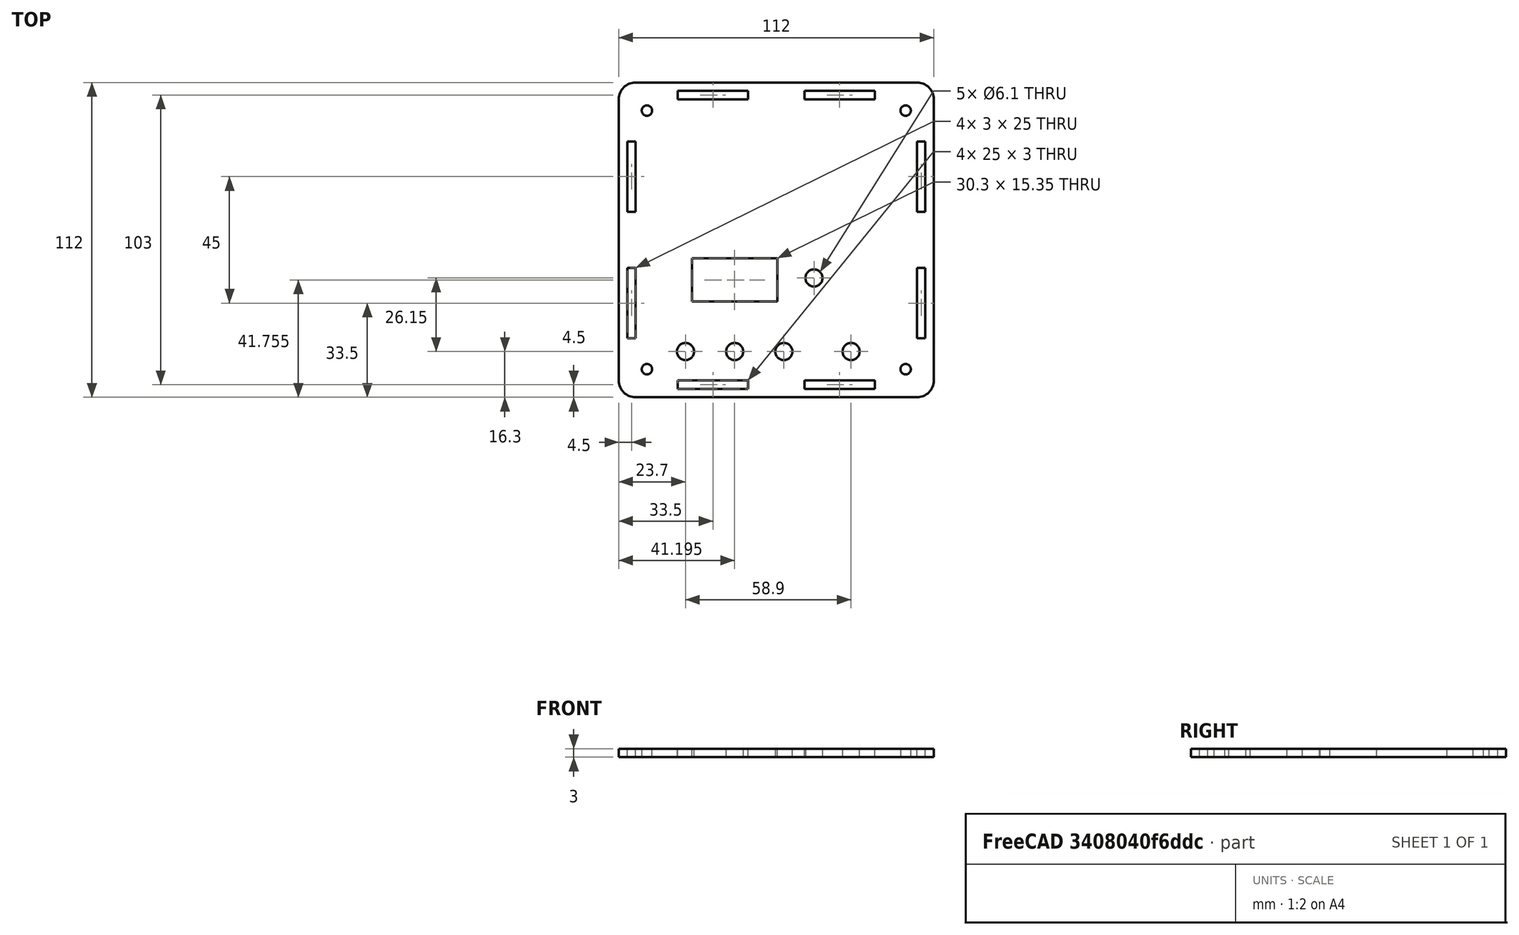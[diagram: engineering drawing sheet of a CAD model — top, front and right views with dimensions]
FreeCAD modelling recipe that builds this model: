
FCSTD DOCUMENT  (FreeCAD 0.19R24267 +99 (Git))
Label: top
License: All rights reserved
LicenseURL: http://en.wikipedia.org/wiki/All_rights_reserved
objects: App::Part×1, Sketcher::SketchObject×1, Part::Extrusion×1
note: 2 computed .brp shape members not serialized (recipe doc carries the construction recipe); baked Part::Feature solids carry a one-line shape summary decoded from their .brp

FEATURE [App::Part] Part
  Origin = -> Origin
FEATURE [Sketcher::SketchObject] Sketch
  FullyConstrained = true
  sketch-geometry (57):
    g0: LineSegment StartX=0 StartY=0 StartZ=0 EndX=100 EndY=0 EndZ=0
    g1: LineSegment StartX=100 StartY=0 StartZ=0 EndX=100 EndY=100 EndZ=0
    g2: LineSegment StartX=100 StartY=100 StartZ=0 EndX=0 EndY=100 EndZ=0
    g3: LineSegment StartX=0 StartY=100 StartZ=0 EndX=0 EndY=0 EndZ=0
    g4: Circle CenterX=17.7 CenterY=10.3 CenterZ=0 NormalX=0 NormalY=0 NormalZ=1 AngleXU=0 Radius=3.05
    g5: Circle CenterX=35.2 CenterY=10.3 CenterZ=0 NormalX=0 NormalY=0 NormalZ=1 AngleXU=0 Radius=3.05
    g6: Circle CenterX=52.7 CenterY=10.3 CenterZ=0 NormalX=0 NormalY=0 NormalZ=1 AngleXU=0 Radius=3.05
    g7: Circle CenterX=76.6 CenterY=10.3 CenterZ=0 NormalX=0 NormalY=0 NormalZ=1 AngleXU=0 Radius=3.05
    g8: Circle CenterX=63.4 CenterY=36.45 CenterZ=0 NormalX=0 NormalY=0 NormalZ=1 AngleXU=0 Radius=3.05
    g9: LineSegment StartX=20.045 StartY=43.43 StartZ=0 EndX=50.345 EndY=43.43 EndZ=0
    g10: LineSegment StartX=50.345 StartY=43.43 StartZ=0 EndX=50.345 EndY=28.08 EndZ=0
    g11: LineSegment StartX=50.345 StartY=28.08 StartZ=0 EndX=20.045 EndY=28.08 EndZ=0
    g12: LineSegment StartX=20.045 StartY=28.08 StartZ=0 EndX=20.045 EndY=43.43 EndZ=0
    g13: ArcOfCircle CenterX=0 CenterY=100 CenterZ=0 NormalX=0 NormalY=0 NormalZ=1 AngleXU=0 Radius=6 StartAngle=1.5708 EndAngle=3.14159
    g14: ArcOfCircle CenterX=100 CenterY=100 CenterZ=0 NormalX=0 NormalY=0 NormalZ=1 AngleXU=0 Radius=6 StartAngle=0 EndAngle=1.5708
    g15: LineSegment StartX=0 StartY=106 StartZ=0 EndX=100 EndY=106 EndZ=0
    g16: Circle CenterX=4 CenterY=96 CenterZ=0 NormalX=0 NormalY=0 NormalZ=1 AngleXU=0 Radius=1.85
    g17: Circle CenterX=96 CenterY=96 CenterZ=0 NormalX=0 NormalY=0 NormalZ=1 AngleXU=0 Radius=1.85
    g18: Circle CenterX=96 CenterY=4 CenterZ=0 NormalX=0 NormalY=0 NormalZ=1 AngleXU=0 Radius=1.85
    g19: Circle CenterX=4 CenterY=4 CenterZ=0 NormalX=0 NormalY=0 NormalZ=1 AngleXU=0 Radius=1.85
    g20: ArcOfCircle CenterX=0 CenterY=0 CenterZ=0 NormalX=0 NormalY=0 NormalZ=1 AngleXU=0 Radius=6 StartAngle=3.14159 EndAngle=4.71239
    g21: ArcOfCircle CenterX=100 CenterY=0 CenterZ=0 NormalX=0 NormalY=0 NormalZ=1 AngleXU=0 Radius=6 StartAngle=4.71239 EndAngle=6.28319
    g22: LineSegment StartX=0 StartY=-6 StartZ=0 EndX=100 EndY=-6 EndZ=0
    g23: LineSegment StartX=106 StartY=-1.5e-15 StartZ=0 EndX=106 EndY=100 EndZ=0
    g24: LineSegment StartX=-6 StartY=100 StartZ=0 EndX=-6 EndY=0 EndZ=0
    g25: LineSegment StartX=15 StartY=100 StartZ=0 EndX=40 EndY=100 EndZ=0
    g26: LineSegment StartX=40 StartY=100 StartZ=0 EndX=40 EndY=103 EndZ=0
    g27: LineSegment StartX=40 StartY=103 StartZ=0 EndX=15 EndY=103 EndZ=0
    g28: LineSegment StartX=15 StartY=103 StartZ=0 EndX=15 EndY=100 EndZ=0
    g29: LineSegment StartX=60 StartY=100 StartZ=0 EndX=85 EndY=100 EndZ=0
    g30: LineSegment StartX=85 StartY=100 StartZ=0 EndX=85 EndY=103 EndZ=0
    g31: LineSegment StartX=85 StartY=103 StartZ=0 EndX=60 EndY=103 EndZ=0
    g32: LineSegment StartX=60 StartY=103 StartZ=0 EndX=60 EndY=100 EndZ=0
    g33: LineSegment StartX=100 StartY=85 StartZ=0 EndX=103 EndY=85 EndZ=0
    g34: LineSegment StartX=103 StartY=85 StartZ=0 EndX=103 EndY=60 EndZ=0
    g35: LineSegment StartX=103 StartY=60 StartZ=0 EndX=100 EndY=60 EndZ=0
    g36: LineSegment StartX=100 StartY=60 StartZ=0 EndX=100 EndY=85 EndZ=0
    g37: LineSegment StartX=100 StartY=40 StartZ=0 EndX=103 EndY=40 EndZ=0
    g38: LineSegment StartX=103 StartY=40 StartZ=0 EndX=103 EndY=15 EndZ=0
    g39: LineSegment StartX=103 StartY=15 StartZ=0 EndX=100 EndY=15 EndZ=0
    g40: LineSegment StartX=100 StartY=15 StartZ=0 EndX=100 EndY=40 EndZ=0
    g41: LineSegment StartX=85 StartY=0 StartZ=0 EndX=60 EndY=0 EndZ=0
    g42: LineSegment StartX=60 StartY=0 StartZ=0 EndX=60 EndY=-3 EndZ=0
    g43: LineSegment StartX=60 StartY=-3 StartZ=0 EndX=85 EndY=-3 EndZ=0
    g44: LineSegment StartX=85 StartY=-3 StartZ=0 EndX=85 EndY=0 EndZ=0
    g45: LineSegment StartX=40 StartY=0 StartZ=0 EndX=15 EndY=0 EndZ=0
    g46: LineSegment StartX=15 StartY=0 StartZ=0 EndX=15 EndY=-3 EndZ=0
    g47: LineSegment StartX=15 StartY=-3 StartZ=0 EndX=40 EndY=-3 EndZ=0
    g48: LineSegment StartX=40 StartY=-3 StartZ=0 EndX=40 EndY=0 EndZ=0
    g49: LineSegment StartX=0 StartY=15 StartZ=0 EndX=-3 EndY=15 EndZ=0
    g50: LineSegment StartX=-3 StartY=15 StartZ=0 EndX=-3 EndY=40 EndZ=0
    g51: LineSegment StartX=-3 StartY=40 StartZ=0 EndX=0 EndY=40 EndZ=0
    g52: LineSegment StartX=0 StartY=40 StartZ=0 EndX=0 EndY=15 EndZ=0
    g53: LineSegment StartX=0 StartY=85 StartZ=0 EndX=-3 EndY=85 EndZ=0
    g54: LineSegment StartX=-3 StartY=85 StartZ=0 EndX=-3 EndY=60 EndZ=0
    g55: LineSegment StartX=-3 StartY=60 StartZ=0 EndX=0 EndY=60 EndZ=0
    g56: LineSegment StartX=0 StartY=60 StartZ=0 EndX=0 EndY=85 EndZ=0
  constraints (170):
    c: Coincident(g0,g1)
    c: Coincident(g1,g2)
    c: Coincident(g2,g3)
    c: Coincident(g3,g0)
    c: Horizontal(g0)
    c: Horizontal(g2)
    c: Vertical(g1)
    c: Vertical(g3)
    c: Coincident(g0,g-1)
    c: DistanceX(g2,g2) = 100
    c: DistanceY(g1,g1) = 100
    c: Coincident(g9,g10)
    c: Coincident(g10,g11)
    c: Coincident(g11,g12)
    c: Coincident(g12,g9)
    c: Horizontal(g9)
    c: Horizontal(g11)
    c: Vertical(g10)
    c: Vertical(g12)
    c: DistanceX(g9,g9) = 30.3
    c: DistanceY(g12,g12) = 15.35
    c: DistanceX(g2,g9) = 20.045
    c: DistanceY(g9,g2) = 56.57
    c: Equal(g4,g5)
    c: Equal(g5,g6)
    c: Equal(g6,g7)
    c: DistanceX(g2,g8) = 63.4
    c: DistanceY(g8,g2) = 63.55
    c: Horizontal(g4,g5)
    c: Horizontal(g5,g6)
    c: Horizontal(g6,g7)
    c: DistanceX(g2,g4) = 17.7
    c: DistanceY(g4,g2) = 89.7
    c: DistanceX(g4,g5) = 17.5
    c: DistanceX(g5,g6) = 17.5
    c: DistanceX(g6,g7) = 23.9
    c: Radius(g8) = 3.05
    c: Radius(g7) = 3.05
    c: Coincident(g13,g2)
    c: PointOnObject(g13,g-2)
    c: Horizontal(g13,g13)
    c: Radius(g13) = 6
    c: Coincident(g14,g1)
    c: Radius(g14) = 6
    c: Vertical(g14,g14)
    c: Horizontal(g14,g14)
    c: Coincident(g15,g13)
    c: Coincident(g15,g14)
    c: Equal(g17,g16)
    c: Equal(g16,g19)
    c: Equal(g19,g18)
    c: Radius(g16) = 1.85
    c: Horizontal(g16,g17)
    c: Horizontal(g19,g18)
    c: Vertical(g19,g16)
    c: Vertical(g17,g18)
    c: DistanceX(g13,g16) = 4
    c: DistanceY(g16,g13) = 4
    c: DistanceY(g-1,g19) = 4
    c: DistanceX(g17,g14) = 4
    c: Coincident(g20,g-1)
    c: PointOnObject(g20,g-1)
    c: PointOnObject(g20,g-2)
    c: Radius(g20) = 6
    c: Coincident(g21,g0)
    c: PointOnObject(g21,g-1)
    c: Radius(g21) = 6
    c: Vertical(g21,g21)
    c: Coincident(g22,g20)
    c: Coincident(g22,g21)
    c: Coincident(g23,g21)
    c: Coincident(g23,g14)
    c: Coincident(g24,g13)
    c: Coincident(g24,g20)
    c: Coincident(g25,g26)
    c: Coincident(g26,g27)
    c: Coincident(g27,g28)
    c: Coincident(g28,g25)
    c: Horizontal(g25)
    c: Horizontal(g27)
    c: Vertical(g26)
    c: Vertical(g28)
    c: PointOnObject(g25,g2)
    c: Coincident(g29,g30)
    c: Coincident(g30,g31)
    c: Coincident(g31,g32)
    c: Coincident(g32,g29)
    c: Horizontal(g29)
    c: Horizontal(g31)
    c: Vertical(g30)
    c: Vertical(g32)
    c: PointOnObject(g29,g2)
    c: Coincident(g33,g34)
    c: Coincident(g34,g35)
    c: Coincident(g35,g36)
    c: Coincident(g36,g33)
    c: Horizontal(g33)
    c: Horizontal(g35)
    c: Vertical(g34)
    c: Vertical(g36)
    c: PointOnObject(g33,g1)
    c: Coincident(g37,g38)
    c: Coincident(g38,g39)
    c: Coincident(g39,g40)
    c: Coincident(g40,g37)
    c: Horizontal(g37)
    c: Horizontal(g39)
    c: Vertical(g38)
    c: Vertical(g40)
    c: PointOnObject(g37,g1)
    c: Coincident(g41,g42)
    c: Coincident(g42,g43)
    c: Coincident(g43,g44)
    c: Coincident(g44,g41)
    c: Horizontal(g41)
    c: Horizontal(g43)
    c: Vertical(g42)
    c: Vertical(g44)
    c: PointOnObject(g41,g0)
    c: Coincident(g45,g46)
    c: Coincident(g46,g47)
    c: Coincident(g47,g48)
    c: Coincident(g48,g45)
    c: Horizontal(g45)
    c: Horizontal(g47)
    c: Vertical(g46)
    c: Vertical(g48)
    c: PointOnObject(g45,g0)
    c: Coincident(g49,g50)
    c: Coincident(g50,g51)
    c: Coincident(g51,g52)
    c: Coincident(g52,g49)
    c: Horizontal(g49)
    c: Horizontal(g51)
    c: Vertical(g50)
    c: Vertical(g52)
    c: Coincident(g53,g54)
    c: Coincident(g54,g55)
    c: Coincident(g55,g56)
    c: Coincident(g56,g53)
    c: Horizontal(g53)
    c: Horizontal(g55)
    c: Vertical(g54)
    c: Vertical(g56)
    c: PointOnObject(g53,g3)
    c: Equal(g28,g32)
    c: Equal(g32,g53)
    c: Equal(g53,g33)
    c: Equal(g33,g37)
    c: Equal(g37,g51)
    c: Equal(g51,g48)
    c: Equal(g48,g42)
    c: DistanceY(g48,g48) = 3
    c: Equal(g47,g43)
    c: Equal(g43,g38)
    c: Equal(g38,g50)
    c: Equal(g50,g34)
    c: Equal(g34,g54)
    c: Equal(g54,g27)
    c: Equal(g27,g31)
    c: DistanceX(g27,g27) = 25
    c: DistanceX(g13,g27) = 15
    c: DistanceX(g30,g14) = 15
    c: DistanceY(g33,g14) = 15
    c: DistanceY(g21,g39) = 15
    c: DistanceX(g43,g21) = 15
    c: DistanceX(g20,g46) = 15
    c: DistanceY(g20,g49) = 15
    c: DistanceY(g53,g13) = 15
    c: PointOnObject(g49,g3)
FEATURE [Part::Extrusion] Extrude
  Base = -> Sketch
  Dir = (0,0,1)
  DirMode = 2
  FaceMakerClass = Part::FaceMakerBullseye
  LengthFwd = 3
  LengthRev = 0
  Solid = true
  Symmetric = false
